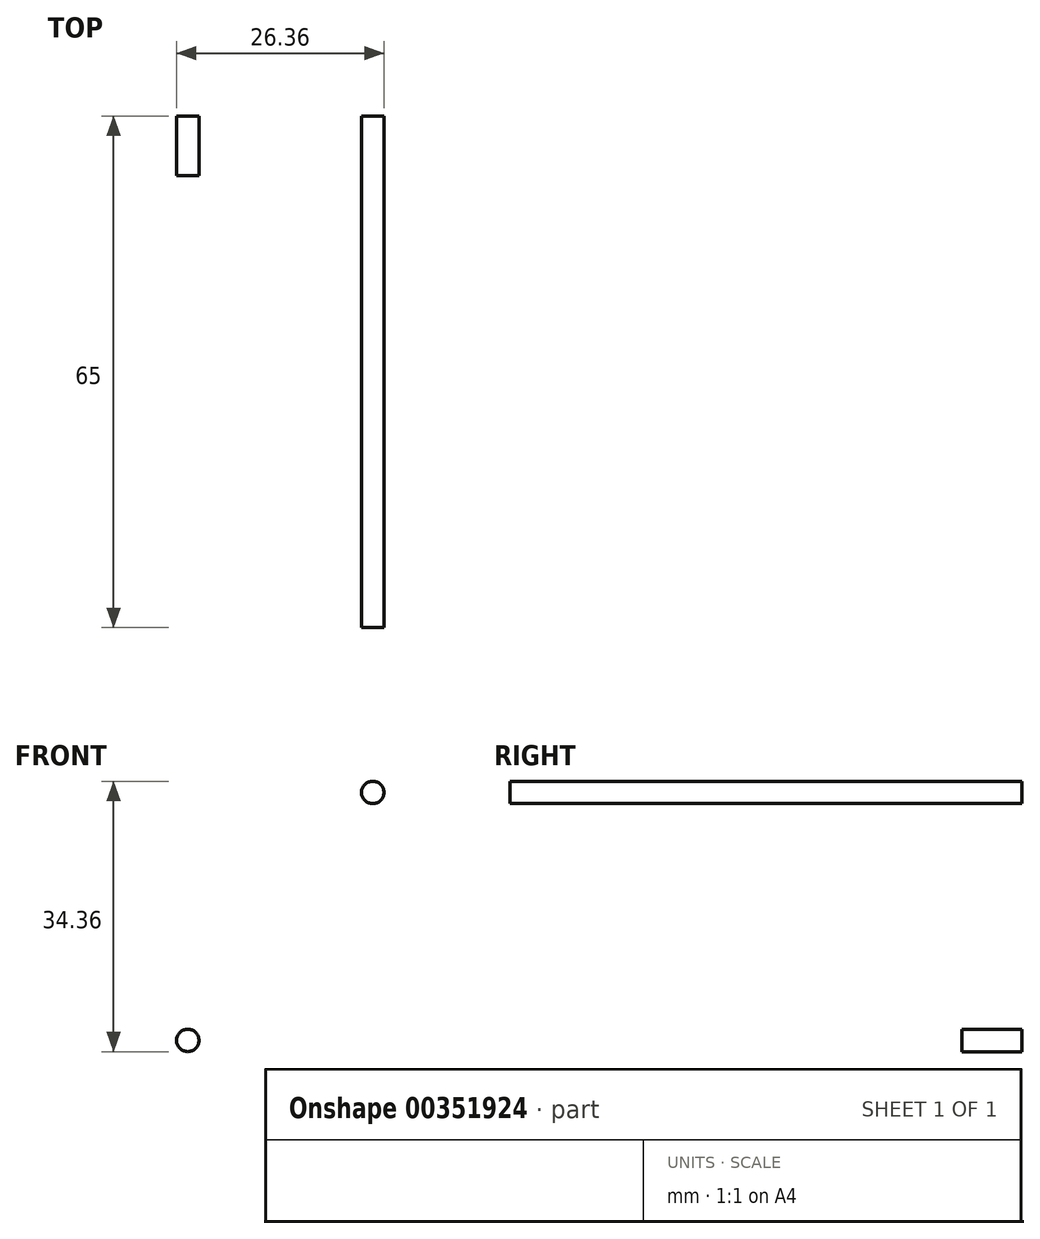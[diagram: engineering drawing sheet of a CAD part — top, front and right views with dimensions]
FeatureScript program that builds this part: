
annotation { "Feature Type Name" : "Feature", "Feature Type Description" : "" }
export const myFeature = defineFeature(function(context is Context, id is Id, definition is map)
    precondition{}
    {
        {
            var Q0;
            Q0=qCreatedBy(makeId("Front.planeOp"),FACE);
            var sketch = newSketch(context, id + "F0", { "sketchPlane" : qUnion([Q0])});
            skCircle(sketch, "E0", {"center": v(0, 0) * mm, "radius": 1.43 * mm});
            skSolve(sketch);
        }
        {
            var Q0;
            Q0 = qSketchRegion(id + "F0", true);
            extrude(context, id + "F1", {"entities" : qUnion([Q0]), "depth" : 65 * mm});
        }
        {
            var Q0;
            Q0=makeQuery(id+"F1.opExtrude","SWEPT_BODY",BODY,{"disambiguationData":[OSD([sQuery(id+"F0.wireOp",EDGE,"E0")])]});
            transform(context, id + "F2", {"entities" : qUnion([Q0]), "transformType" : TransformType.TRANSLATION_3D, "dx" : 23.5 * mm, "dy" : 0 * mm, "dz" : 31.5 * mm, "makeCopy" : false});
        }
        {
            var Q0;
            Q0 = qSketchRegion(id + "F0", true);
            extrude(context, id + "F3", {"entities" : qUnion([Q0]), "depth" : 7.6 * mm});
        }
    });
